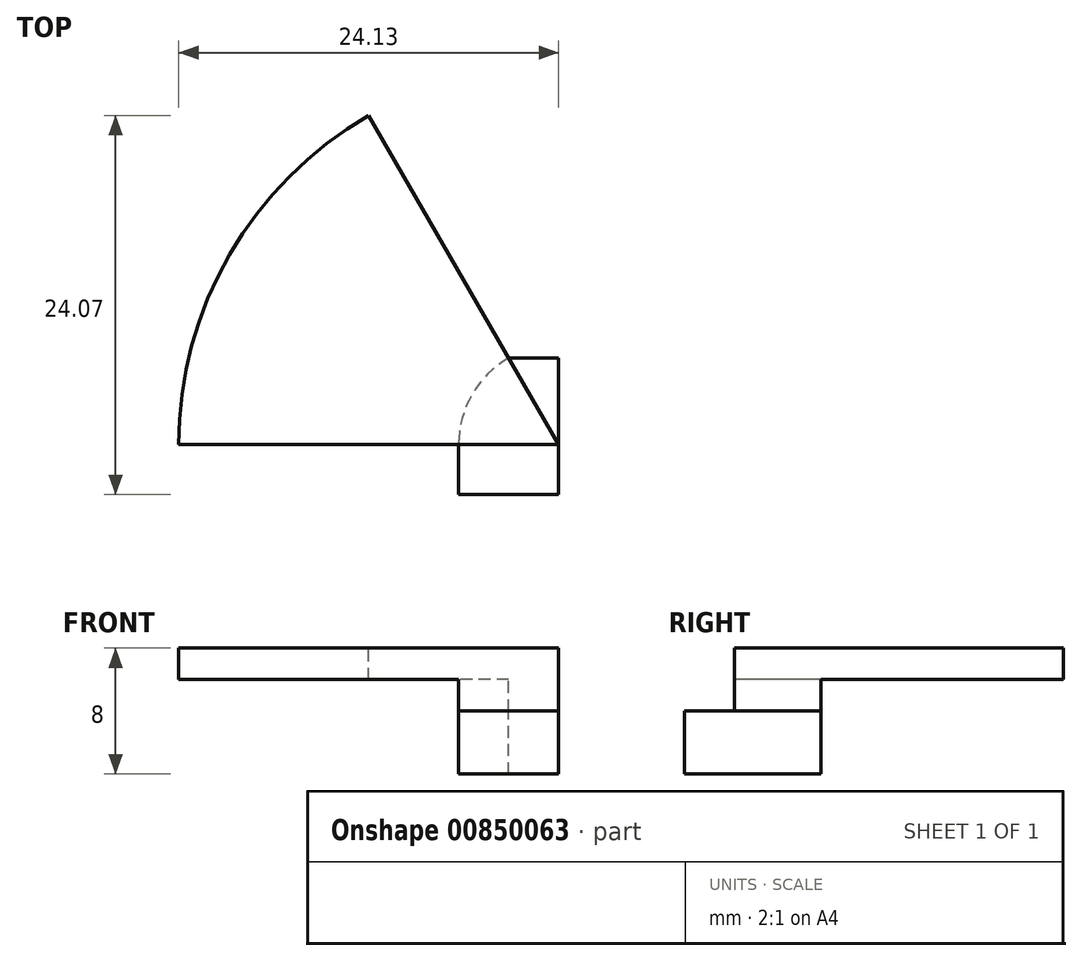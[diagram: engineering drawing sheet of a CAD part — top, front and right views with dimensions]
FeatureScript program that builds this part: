
annotation { "Feature Type Name" : "Feature", "Feature Type Description" : "" }
export const myFeature = defineFeature(function(context is Context, id is Id, definition is map)
    precondition{}
    {
        {
            var Q0;
            Q0=qCreatedBy(makeId("Front.planeOp"),FACE);
            var sketch = newSketch(context, id + "F0", { "sketchPlane" : qUnion([Q0])});
            skLineSegment(sketch, "E0", {"start": v(0, 0) * mm, "end": v(0, 6) * mm});
            skLineSegment(sketch, "E1", {"start": v(0, 6) * mm, "end": v(-17.78, 6) * mm});
            skLineSegment(sketch, "E2", {"start": v(-17.78, 6) * mm, "end": v(-17.78, 8) * mm});
            skLineSegment(sketch, "E3", {"start": v(-17.78, 8) * mm, "end": v(6.35, 8) * mm});
            skLineSegment(sketch, "E4", {"start": v(6.35, 8) * mm, "end": v(6.35, 0) * mm});
            skLineSegment(sketch, "E5", {"start": v(6.35, 0) * mm, "end": v(0, 0) * mm});
            skSolve(sketch);
        }
        {
            var Q0;
            Q0=makeQuery(id+"F0.imprint","IMPRINT",FACE,{"disambiguationData":[TD([[makeQuery(id+"F0.imprint","IMPRINT",EDGE,{"derivedFrom":sQuery(id+"F0.wireOp",EDGE,"E0")}),-1.0]])]});
            var Q1;
            Q1=sQuery(id+"F0.wireOp",EDGE,"E4");
            revolve(context, id + "F1", {"surfaceOperationType" : NewSurfaceOperationType.NEW, "entities" : qUnion([Q0]), "axis" : qUnion([Q1]), "revolveType" : RevolveType.ONE_DIRECTION, "angle" : 60 * degree});
        }
        {
            var Q0;
            Q0=makeQuery(id+"F1.opRevolve","SWEPT_FACE",FACE,{"disambiguationData":[OSD([sQuery(id+"F0.wireOp",EDGE,"E5")])]});
            var sketch = newSketch(context, id + "F2", { "sketchPlane" : qUnion([Q0])});
            skLineSegment(sketch, "E6", {"start": v(0, 0) * mm, "end": v(0, 3.17) * mm});
            skLineSegment(sketch, "E7", {"start": v(0, 3.17) * mm, "end": v(6.35, 3.18) * mm});
            skLineSegment(sketch, "E8", {"start": v(6.35, 3.17) * mm, "end": v(6.35, -5.5) * mm});
            skLineSegment(sketch, "E9", {"start": v(6.35, -5.5) * mm, "end": v(3.17, -5.5) * mm});
            skSolve(sketch);
        }
        {
            var Q0;
            Q0=makeQuery(id+"F2.imprint","IMPRINT",FACE,{"disambiguationData":[TD([[makeQuery(id+"F2.imprint","IMPRINT",EDGE,{"derivedFrom":sQuery(id+"F2.wireOp",EDGE,"E6")}),-1.0]])]});
            var Q1;
            {var subQ3=sQuery(id+"F2.wireOp",EDGE,"E9");Q1=makeQuery(id+"F2.imprint","IMPRINT",FACE,{"disambiguationData":[TD([[makeQuery(id+"F2.imprint","IMPRINT",EDGE,{"derivedFrom":subQ3}),-1.0]])]});}
            extrude(context, id + "F3", {"entities" : qUnion([Q0, Q1]), "operationType" : NewBodyOperationType.ADD, "oppositeDirection" : true, "depth" : 4 * mm, "offsetDistance" : 25.4 * mm});
        }
    });
